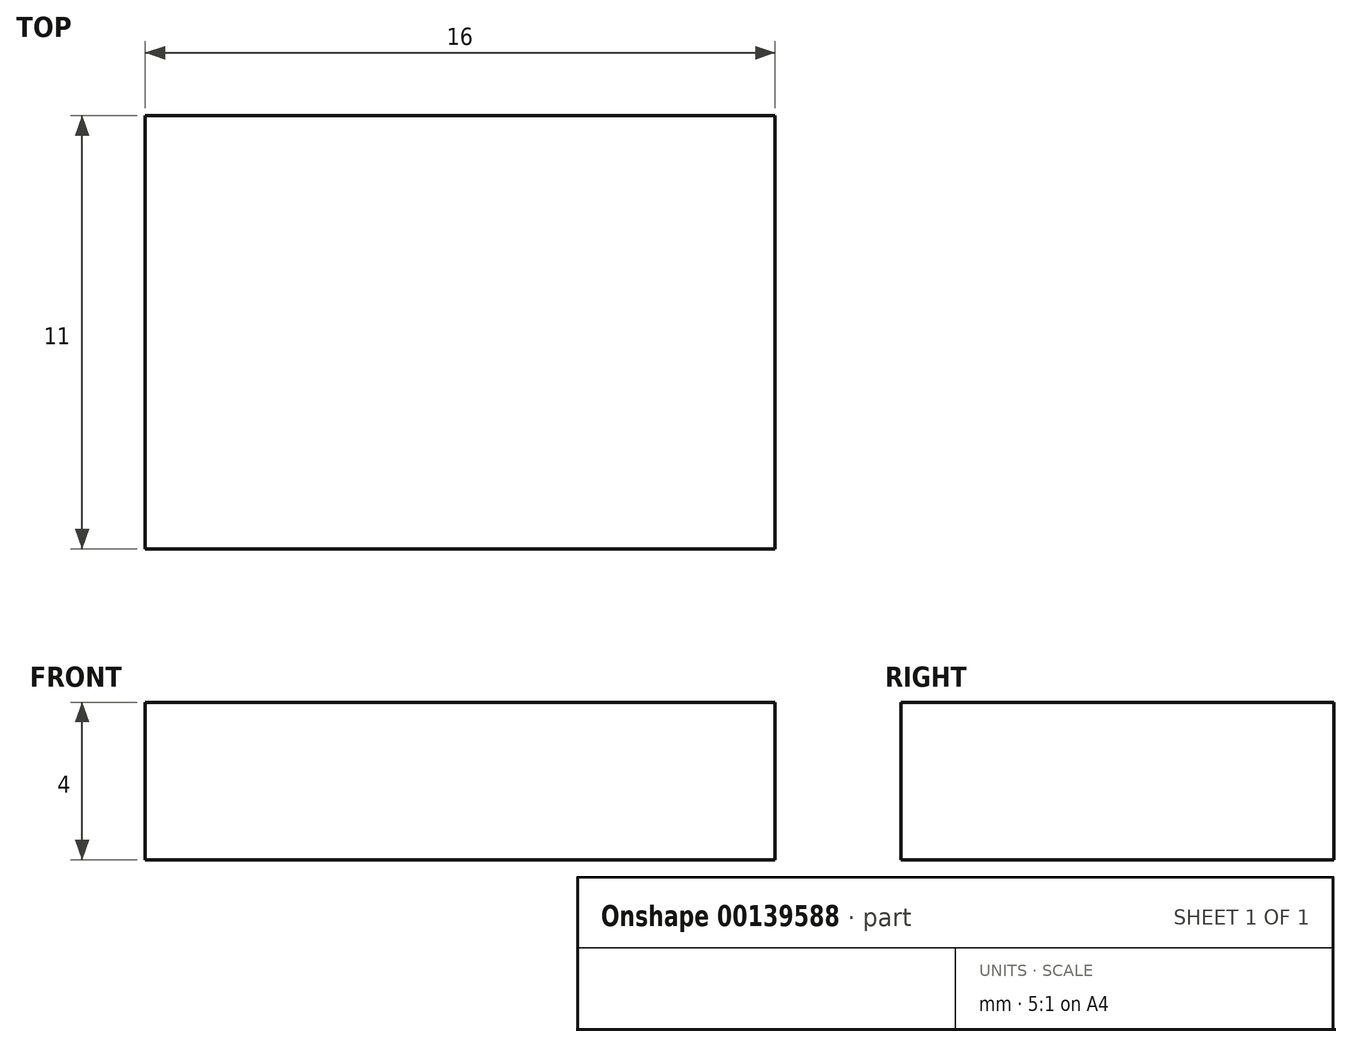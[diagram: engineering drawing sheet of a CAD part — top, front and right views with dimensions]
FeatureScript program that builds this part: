
annotation { "Feature Type Name" : "Feature", "Feature Type Description" : "" }
export const myFeature = defineFeature(function(context is Context, id is Id, definition is map)
    precondition{}
    {
        {
            var Q0;
            Q0=qCreatedBy(makeId("Front.planeOp"),FACE);
            var sketch = newSketch(context, id + "F0", { "sketchPlane" : qUnion([Q0])});
            skLineSegment(sketch, "E0.bottom", {"start": v(-8, 2) * mm, "end": v(8, 2) * mm});
            skLineSegment(sketch, "E0.top", {"start": v(-8, -2) * mm, "end": v(8, -2) * mm});
            skLineSegment(sketch, "E0.left", {"start": v(-8, 2) * mm, "end": v(-8, -2) * mm});
            skLineSegment(sketch, "E0.right", {"start": v(8, 2) * mm, "end": v(8, -2) * mm});
            skPoint(sketch, "E0.middle", {"position": v(0, 0) * mm});
            skSolve(sketch);
        }
        {
            var Q0;
            Q0 = qSketchRegion(id + "F0", true);
            extrude(context, id + "F1", {"entities" : qUnion([Q0]), "endBound" : BoundingType.SYMMETRIC, "depth" : 11 * mm});
        }
    });
